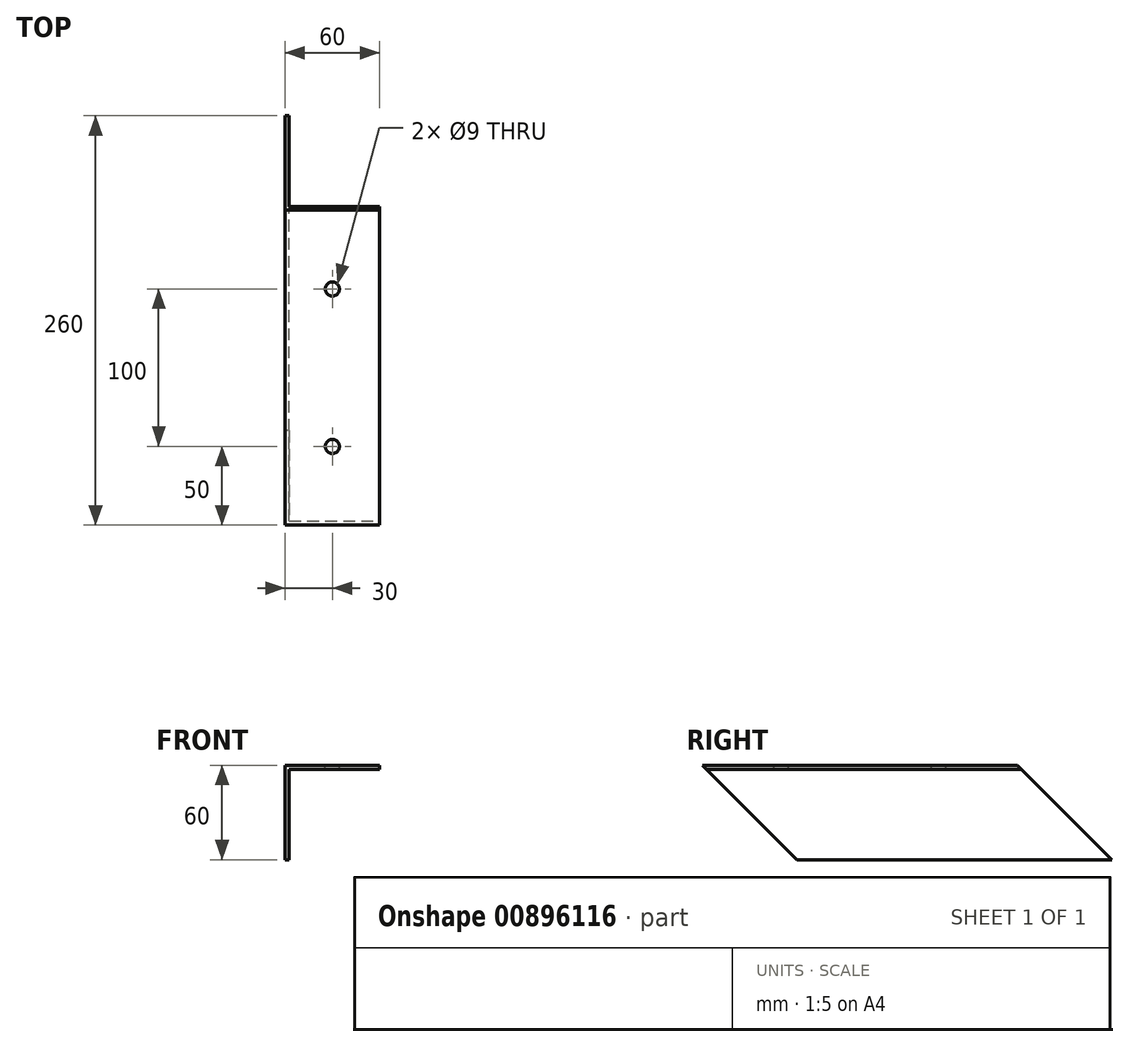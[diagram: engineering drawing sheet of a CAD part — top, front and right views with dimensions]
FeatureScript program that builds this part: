
annotation { "Feature Type Name" : "Feature", "Feature Type Description" : "" }
export const myFeature = defineFeature(function(context is Context, id is Id, definition is map)
    precondition{}
    {
        {
            var Q0;
            Q0=qCreatedBy(makeId("Front.planeOp"),FACE);
            var sketch = newSketch(context, id + "F0", { "sketchPlane" : qUnion([Q0])});
            skLineSegment(sketch, "E0", {"start": v(0, 0) * mm, "end": v(60, 0) * mm});
            skLineSegment(sketch, "E1", {"start": v(60, 0) * mm, "end": v(60, -2.5) * mm});
            skLineSegment(sketch, "E2", {"start": v(60, -2.5) * mm, "end": v(2.5, -2.5) * mm});
            skLineSegment(sketch, "E3", {"start": v(2.5, -2.5) * mm, "end": v(2.5, -60) * mm});
            skLineSegment(sketch, "E4", {"start": v(2.5, -60) * mm, "end": v(0, -60) * mm});
            skLineSegment(sketch, "E5", {"start": v(0, -60) * mm, "end": v(0, 0) * mm});
            skSolve(sketch);
        }
        {
            var Q0;
            Q0=qSketchRegion(id+"F0",true);
            extrude(context, id + "F1", {"entities" : qUnion([Q0]), "depth" : 260 * mm, "offsetDistance" : 25 * mm});
        }
        {
            var Q0;
            Q0=makeQuery(id+"F1.opExtrude","SWEPT_FACE",FACE,{"disambiguationData":[OSD([sQuery(id+"F0.wireOp",EDGE,"E5")])]});
            var sketch = newSketch(context, id + "F2", { "sketchPlane" : qUnion([Q0])});
            skLineSegment(sketch, "E6", {"start": v(0, -60) * mm, "end": v(60, 0) * mm});
            skLineSegment(sketch, "E7", {"start": v(60, 0) * mm, "end": v(0, 0) * mm});
            skLineSegment(sketch, "E8", {"start": v(0, 0) * mm, "end": v(0, -60) * mm});
            skLineSegment(sketch, "E9", {"start": v(260, 0) * mm, "end": v(200, -60) * mm});
            skLineSegment(sketch, "E10", {"start": v(200, -60) * mm, "end": v(260, -60) * mm});
            skLineSegment(sketch, "E11", {"start": v(260, -60) * mm, "end": v(260, 0) * mm});
            skSolve(sketch);
        }
        {
            var Q0;
            Q0 = qSketchRegion(id + "F2", true);
            extrude(context, id + "F3", {"entities" : qUnion([Q0]), "operationType" : NewBodyOperationType.REMOVE, "endBound" : BoundingType.THROUGH_ALL, "oppositeDirection" : true, "depth" : 25 * mm, "offsetDistance" : 25 * mm});
        }
        {
            var Q0;
            Q0=makeQuery(id+"F1.opExtrude","SWEPT_FACE",FACE,{"disambiguationData":[OSD([sQuery(id+"F0.wireOp",EDGE,"E0")])]});
            var sketch = newSketch(context, id + "F4", { "sketchPlane" : qUnion([Q0])});
            skLineSegment(sketch, "E12", {"start": v(30, -60) * mm, "end": v(30, -110) * mm, "construction": true});
            skLineSegment(sketch, "E13", {"start": v(30, -110) * mm, "end": v(30, -210) * mm, "construction": true});
            skLineSegment(sketch, "E14", {"start": v(30, -210) * mm, "end": v(30, -260) * mm, "construction": true});
            skCircle(sketch, "E15", {"center": v(30, -110) * mm, "radius": 4.5 * mm});
            skCircle(sketch, "E16", {"center": v(30, -210) * mm, "radius": 4.5 * mm});
            skSolve(sketch);
        }
        {
            var Q0;
            Q0 = qSketchRegion(id + "F4", true);
            extrude(context, id + "F5", {"entities" : qUnion([Q0]), "operationType" : NewBodyOperationType.REMOVE, "endBound" : BoundingType.THROUGH_ALL, "oppositeDirection" : true, "depth" : 25 * mm, "offsetDistance" : 25 * mm});
        }
    });
